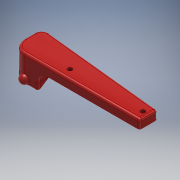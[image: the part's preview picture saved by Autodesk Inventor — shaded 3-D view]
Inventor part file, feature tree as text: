
AUTODESK INVENTOR PART (.ipt)
format: ipt  version: 2018.3 (Build 223284000, 284)  size: 250,368 bytes
history: native  units: mm
features: fillet x6, extrude x4, sketch x4, plane x1, chamfer x1, revolve x1
ambient origin geometry x8: Origin, YZ Plane, XZ Plane, XY Plane, X Axis, Y Axis, Z Axis, Center Point
bodies: Solid1 (feature_tree)
feature tree (17):
  extrude  "Extrusion1"  Depth=14.0mm
  extrude  "Extrusion2"  Depth=2.0mm
  extrude  "Extrusion3"  Depth=33.0mm
  plane  "Work Plane1"
  fillet  "Fillet1"  Radius=3.0mm
  chamfer  "Chamfer1"  Distance=12.0mm
  revolve  "Revolution2"  [1 undecoded]
  fillet  "Fillet6"  Radius=4.0mm
  fillet  "Fillet7"  Radius=6.0mm
  fillet  "Fillet8"  Radius=4.0mm
  fillet  "Fillet9"  Radius=3.0mm
  extrude  "Extrusion4"  TaperAngle=180.0deg  [1 undecoded]
  fillet  "Fillet10"  Radius=3.0mm
  sketch  "Sketch1"  dims[d0=58.0mm d1=14.0mm]
  sketch  "Sketch2"  dims[d2=4.0mm d3=0.0mm d4=2.0mm]
  sketch  "Sketch3"  dims[d6=2.0mm d7=33.0mm d8=3.0mm d9=0.0mm]
  sketch  "Sketch6"  dims[d10=9.0mm d11=12.0mm d12=0.0mm d17=6.0mm d22=4.0mm d23=6.0mm d24=58.0mm d25=45.0deg d26=4.0mm d27=3.0mm d28=180.0deg d29=3.0mm d30=1.0mm d31=1.0mm d32=1.0mm d33=4.0mm d34=1.0mm d35=0.0mm d36=5.0mm]
note: 2 required parameter values undecoded (feature->parameter linkage not recoverable at this tier; creation-order binding heuristic only, values carry confidence <= 0.55)